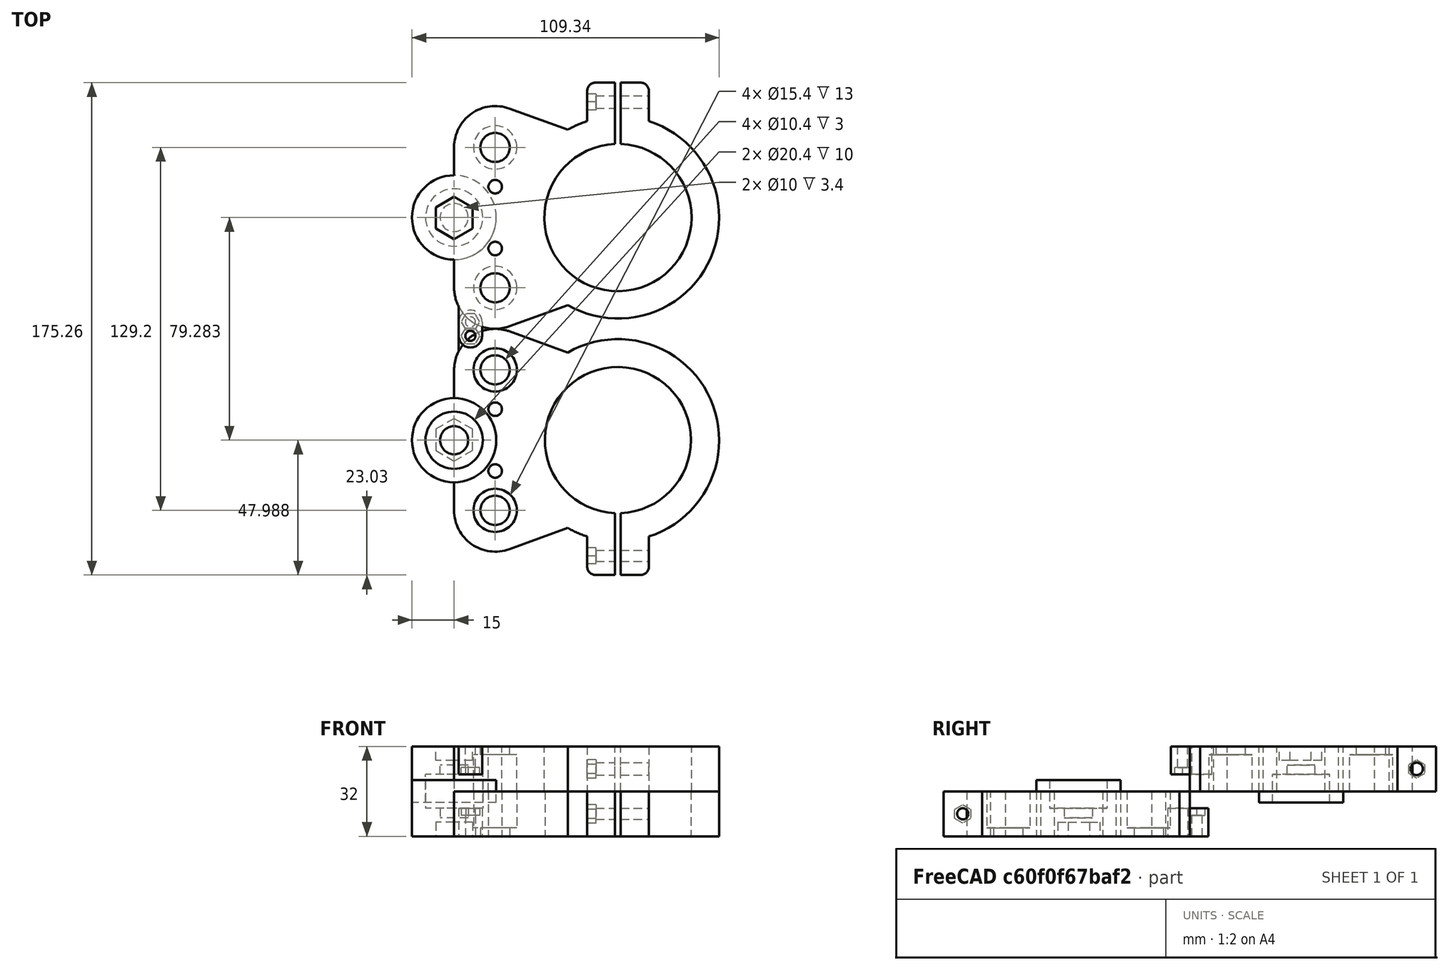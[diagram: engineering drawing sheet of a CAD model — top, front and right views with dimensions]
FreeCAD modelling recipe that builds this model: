
FCSTD DOCUMENT  (FreeCAD 0.15R4664 (Git))
Label: z_spindle_holder_top
License: All rights reserved
LicenseURL: http://en.wikipedia.org/wiki/All_rights_reserved
objects: Part::Cylinder×13, Part::Cut×12, Part::MultiFuse×6, Part::Feature×3, Part::Prism×3, Mesh::Feature×2, Part::Box×2, Sketcher::SketchObject×1, Part::Extrusion×1, Part::Fillet×1
note: 42 computed .brp shape members not serialized (recipe doc carries the construction recipe); baked Part::Feature solids carry a one-line shape summary decoded from their .brp

FEATURE [Mesh::Feature] spindleholderantibacklash
FEATURE [Part::Feature] spindleholderantibacklash001001  label="spindleholderantibacklash002"
  shape: bbox 94.34 x 87.63 x 16 mm, 1291 faces, 0 solids (baked)
FEATURE [Sketcher::SketchObject] Sketch
  ExternalGeometry = -> [spindleholderantibacklash001001]
  Placement = pos=(0,0,16) rot=(1,0,0;3.14159rad)
  Support = -> spindleholderantibacklash001001 [Face5]
  sketch-geometry (13):
    g0: ArcOfCircle [constr] CenterX=14.6467 CenterY=-64.6499 CenterZ=0 NormalX=0 NormalY=0 NormalZ=1 Radius=14.65 StartAngle=2.12021 EndAngle=5.06145
    g1: ArcOfCircle [constr] CenterX=14.6467 CenterY=-14.6499 CenterZ=0 NormalX=0 NormalY=0 NormalZ=1 Radius=14.65 StartAngle=1.22173 EndAngle=4.16298
    g2: ArcOfCircle CenterX=58.3467 CenterY=-39.6499 CenterZ=0 NormalX=0 NormalY=0 NormalZ=1 Radius=35.9947 StartAngle=5.02296 EndAngle=8.37543
    g3: ArcOfCircle CenterX=58.3469 CenterY=-39.6492 CenterZ=0 NormalX=0 NormalY=0 NormalZ=1 Radius=35.9954 StartAngle=4.19094 EndAngle=4.40182
    g4: LineSegment StartX=40.4163 StartY=-70.8607 StartZ=0 EndX=19.6573 EndY=-78.4164 EndZ=0
    g5: LineSegment [constr] StartX=6.99666 StartY=-27.1439 StartZ=0 EndX=6.99666 EndY=-52.1559 EndZ=0
    g6: LineSegment StartX=19.6573 StartY=-0.883396 StartZ=0 EndX=40.4163 EndY=-8.43906 EndZ=0
    g7: LineSegment StartX=47.3466 StartY=-73.9226 StartZ=0 EndX=47.3466 EndY=-87.6307 EndZ=0
    g8: LineSegment StartX=69.3466 StartY=-73.9226 StartZ=0 EndX=69.3466 EndY=-87.6307 EndZ=0
    g9: LineSegment StartX=47.3466 StartY=-87.6307 StartZ=0 EndX=69.3466 EndY=-87.6307 EndZ=0
    g10: LineSegment StartX=-0.00333386 StartY=-64.6335 StartZ=0 EndX=-0.00334317 EndY=-14.6499 EndZ=0
    g11: ArcOfCircle CenterX=14.6467 CenterY=-14.6499 CenterZ=0 NormalX=0 NormalY=0 NormalZ=1 Radius=14.65 StartAngle=1.22173 EndAngle=3.14159
    g12: ArcOfCircle CenterX=14.6467 CenterY=-64.6499 CenterZ=0 NormalX=0 NormalY=0 NormalZ=1 Radius=14.65 StartAngle=3.14047 EndAngle=5.06145
  constraints (34):
    c: Coincident(g0,g-3)
    c: Coincident(g0,g-4)
    c: PointOnObject(g-5,g0)
    c: Coincident(g1,g-4)
    c: Coincident(g1,g-13)
    c: PointOnObject(g-14,g1)
    c: Coincident(g2,g-13)
    c: Coincident(g2,g-10)
    c: PointOnObject(g-12,g2)
    c: Coincident(g3,g-3)
    c: Coincident(g3,g-6)
    c: PointOnObject(g-7,g3)
    c: Coincident(g4,g3)
    c: Coincident(g4,g0)
    c: Coincident(g5,g1)
    c: Coincident(g5,g0)
    c: Coincident(g6,g1)
    c: Coincident(g6,g2)
    c: Coincident(g7,g3)
    c: Vertical(g7)
    c: Coincident(g8,g2)
    c: Vertical(g8)
    c: Horizontal(g9)
    c: PointOnObject(g-8,g9)
    c: Coincident(g9,g7)
    c: Coincident(g8,g9)
    c: PointOnObject(g10,g0)
    c: Tangent(g10,g1) = 1.5708
    c: Coincident(g11,g1)
    c: Coincident(g11,g10)
    c: Coincident(g11,g1)
    c: Coincident(g12,g0)
    c: Coincident(g12,g10)
    c: Coincident(g12,g0)
FEATURE [Part::Cylinder] Cylinder  label="Cilindro"
  Angle = 360
  Height = 17
  Placement = pos=(14.6,14.6,-4) rot=(0,0,1;0rad)
  Radius = 7.7
FEATURE [Part::Cylinder] Cylinder001  label="Cilindro001"
  Angle = 360
  Height = 17
  Placement = pos=(14.6,64.6,-4) rot=(0,0,1;0rad)
  Radius = 7.7
FEATURE [Part::MultiFuse] Fusion  label="bearing_holes"
  Shapes = -> [Cylinder,Cylinder001]
FEATURE [Part::Cylinder] Cylinder002  label="Cilindro002"
  Angle = 360
  Height = 17
  Placement = pos=(14.6,28.6,-0.4) rot=(0,0,1;0rad)
  Radius = 2.4
FEATURE [Part::Cylinder] Cylinder003  label="Cilindro003"
  Angle = 360
  Height = 17
  Placement = pos=(14.6,50.6,-0.4) rot=(0,0,1;0rad)
  Radius = 2.4
FEATURE [Part::MultiFuse] Fusion001  label="screw_holes"
  Shapes = -> [Cylinder002,Cylinder003]
FEATURE [Part::Cylinder] Cylinder004  label="Cilindro004"
  Angle = 360
  Height = 17
  Placement = pos=(14.6,14.6,-1) rot=(0,0,1;0rad)
  Radius = 5.2
FEATURE [Part::Cylinder] Cylinder005  label="Cilindro005"
  Angle = 360
  Height = 17
  Placement = pos=(14.6,64.6,-1) rot=(0,0,1;0rad)
  Radius = 5.2
FEATURE [Part::MultiFuse] Fusion003  label="bearing_holes001"
  Shapes = -> [Cylinder004,Cylinder005]
FEATURE [Part::Cylinder] Cylinder006  label="Cilindro006"
  Angle = 360
  Height = 18
  Placement = pos=(58.3,39.6,-1) rot=(0,0,1;0rad)
  Radius = 26.2
FEATURE [Part::Box] Box  label="Cubo"
  Height = 18
  Length = 2
  Placement = pos=(57.3,63,-1) rot=(0,0,1;0rad)
  Width = 27
FEATURE [Part::Cylinder] Cylinder007  label="Cilindro007"
  Angle = 360
  Height = 20
  Placement = pos=(50,80.77,8) rot=(0,1,0;1.5708rad)
  Radius = 2.2
FEATURE [Part::Prism] Prism002  label="Prisma002"
  Circumradius = 3.29
  Height = 4
  Placement = pos=(50.5,80.8,8) rot=(0,-1,0;1.5708rad)
  Polygon = 6
FEATURE [Part::Extrusion] Extrude
  Base = -> Sketch
  Dir = (0,0,-16)
  Solid = true
FEATURE [Mesh::Feature] spindleholdertopantibacklash
  Placement = pos=(-15,87.6,16) rot=(1,0,0;3.14159rad)
FEATURE [Part::Cylinder] Cylinder008  label="Cilindro008"
  Angle = 360
  Height = 20
  Placement = pos=(0,39.6417,-4) rot=(0,0,1;0rad)
  Radius = 15
FEATURE [Part::MultiFuse] Fusion004
  Shapes = -> [Extrude,Cylinder008]
FEATURE [Part::Cut] Cut
  Base = -> Fusion004
  Tool = -> Cylinder006
FEATURE [Part::Cut] Cut001
  Base = -> Cut
  Tool = -> Fusion
FEATURE [Part::Cut] Cut002
  Base = -> Cut001
  Tool = -> Fusion001
FEATURE [Part::Cut] Cut003
  Base = -> Cut002
  Tool = -> Fusion003
FEATURE [Part::Cut] Cut004
  Base = -> Cut003
  Tool = -> Box
FEATURE [Part::Cut] Cut005
  Base = -> Cut004
  Tool = -> Cylinder007
FEATURE [Part::Cut] Cut006
  Base = -> Cut005
  Tool = -> Prism002
FEATURE [Part::Feature] spindleholdertopantibacklash001001  label="spindleholdertopantibacklash002"
  shape: bbox 109.3 x 94.27 x 20 mm, 1536 faces, 0 solids (baked)
FEATURE [Part::Cylinder] Cylinder009  label="Cilindro009"
  Angle = 360
  Height = 11
  Placement = pos=(0,39.6417,-5) rot=(0,0,1;0rad)
  Radius = 10.2
FEATURE [Part::Cylinder] Cylinder010  label="Cilindro010"
  Angle = 360
  Height = 9.4
  Placement = pos=(0,39.6417,0) rot=(0,0,1;0rad)
  Radius = 5
FEATURE [Part::Cut] Cut007
  Base = -> Cut006
  Tool = -> Cylinder009
FEATURE [Part::Cut] Cut008
  Base = -> Cut007
  Tool = -> Cylinder010
FEATURE [Part::Prism] Prism  label="Prisma"
  Circumradius = 7.55
  Height = 6
  Placement = pos=(0,39.467,11) rot=(0,0,1;0.523599rad)
  Polygon = 6
FEATURE [Part::Cut] Cut009
  Base = -> Cut008
  Tool = -> Prism
FEATURE [Part::Fillet] Fillet
  Base = -> Cut009
  Edges = 2 edges r=3: [Edge10,Edge86]
FEATURE [Part::Cylinder] Cylinder011  label="Cilindro011"
  Angle = 360
  Height = 10
  Placement = pos=(5.8,-2.5,6) rot=(0,0,1;0rad)
  Radius = 4.15
FEATURE [Part::Box] Box001  label="Cubo001"
  Height = 10
  Length = 8.3
  Placement = pos=(1.65,-2.5,6) rot=(0,0,1;0rad)
  Width = 10.7
FEATURE [Part::Cylinder] Cylinder012  label="Cilindro012"
  Angle = 360
  Height = 12
  Placement = pos=(5.8,-2.5,5) rot=(0,0,1;0rad)
  Radius = 1.8
FEATURE [Part::MultiFuse] Fusion005
  Shapes = -> [Box001,Cylinder011]
FEATURE [Part::Cut] Cut010
  Base = -> Fusion005
  Tool = -> Cylinder012
FEATURE [Part::Prism] Prism003  label="Prisma003"
  Circumradius = 3.3
  Height = 3
  Placement = pos=(5.8,-2.5,5.5) rot=(0,0,1;0rad)
  Polygon = 6
FEATURE [Part::Cut] Cut011
  Base = -> Cut010
  Tool = -> Prism003
FEATURE [Part::MultiFuse] Fusion006
  Shapes = -> [Cut011,Fillet]
FEATURE [Part::Feature] Fusion006_solid  label="Fusion006 (Solid)"
  Placement = pos=(0,0,0) rot=(1,0,0;3.14159rad)
  shape: bbox 109.3 x 94.28 x 20 mm, 61 faces (baked)
